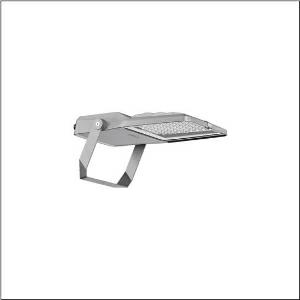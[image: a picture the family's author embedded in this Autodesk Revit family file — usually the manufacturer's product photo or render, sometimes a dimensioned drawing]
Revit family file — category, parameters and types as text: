
# Revit family: floodlight_fl_21_iq_mini___pl61_5xa7772c1c1a_a98f
name_source: partatom
category: Lighting Fixtures
units: mm (PartAtom-declared; Revit-internal decimal feet)

## family parameters
Cut with Voids When Loaded = No
Host = Face
Light Source = No
Part Type = Normal
Room Calculation Point = No
Round Connector Dimension = Use Diameter
Shared = No

## types (1)
- --- (1 x LED, 9930 lm, 87.2 W, 2200K)
    Apparent Load = 87 VA
    CIE Flux Codes = 33 65 98 100 100
    Color Rendering = 70
    Color Temperature = 2200K
    Default Elevation = 1800 mm
    Description = Floodlight FL 21 iQ mini, floodlight, primary light control with lens, of PMMA, primary optical cover: protective disc, of toughened safety glass, transparent, light distribution: PL61, light emission: direct distribution, installation type: surface-mounted, LED, High Power LED, rated luminous flux: 9.930lm, luminous efficacy: 114lm/W, light colour: 722, colour temperature: 2200K, control gear: iQ Street-Remote/DALI, control: Street-Remote, Auto-Match, Temp-Guard, Night-Set, Smart-Wire, Desk-Remote (wireless, voltage-free reading and setting of iQ features in the workshop via application-optimized NFC function/RFID function), optimised constant luminous flux control (CLO 2.0), with terminal, 6-pole, mains connection: 220..240V, AC, 50/60Hz, start of lifetime: 87W, end of service life: 92W, reduction: 40W, luminaire housing, of diecast aluminium, powder-coated, Siteco® metallic grey (DB 702S), corrosivity category C5 mid according to DIN EN ISO 12944, suitable for swimming pools, chlorine-resistant, sealing non-destructively replaceable, mounting bracket, of steel, galvanised, powder-coated, Siteco® metallic grey (DB 702S), protection rating (complete): IP66, insulation class (complete): insulation class II (safety insulation), certification: CE, ENEC, VDE, protection symbol: D, impact resistance: IK08, permissible operating ambient temperature: -40..+40°C, permissible operating ambient temperature for outdoor applications: -40..+50°C, standard: DIN EN 12944, LABS conformity tested according to VDMA 24364:2018-05, packaging unit: 1 piece

Light Distribution: PL61
    Height = 70 mm
    Lamp = 1 x LED
    Lamp Light Flux = 9930 lm
    Lamp Power = 87.2 W
    Lamp count = 1
    Length = 485 mm
    Luminous efficacy = 114 lm/W
    Manufacturer = Siteco
    ModVariant = No
    Model = 5XA7772C1C1A
    Number of Poles = 1
    OnlyDefault = Yes
    Power Factor = 1
    Product Name = Floodlight FL 21 iQ mini | PL61
    Product group = floodlight | pylon annexe
    ProductGroupID = 6201
    Protection Class = Protection class II
    Protection Degree = IP 66
    RLX_Detail_Level = 1
    RLX_Emergency_Light_Flux = 0 lm
    RLX_Emergency_Type = 0
    RLX_Emergency_Type_DB = No
    RlxData = <blob elided: 96317 chars, md5=da88d5f6>
    Socket = socket
    Standby Power = 0 W
    System Light Flux = 9930 lm
    System Power = 87 W
    Type Comments = factory setting: luminous flux: 100 % | dim-lin: 254 | 456 mA
    Type Image = l_1006845.jpg
    URL = http://relux.com
    VarID = @adj_194625
    Voltage = 0 V
    Weight = 0.00 kg
    Width = 337 mm

## geometry (parser evidence)
native form markers: Blend x4, Sweep x11
no freeform markers — native parametric forms only
